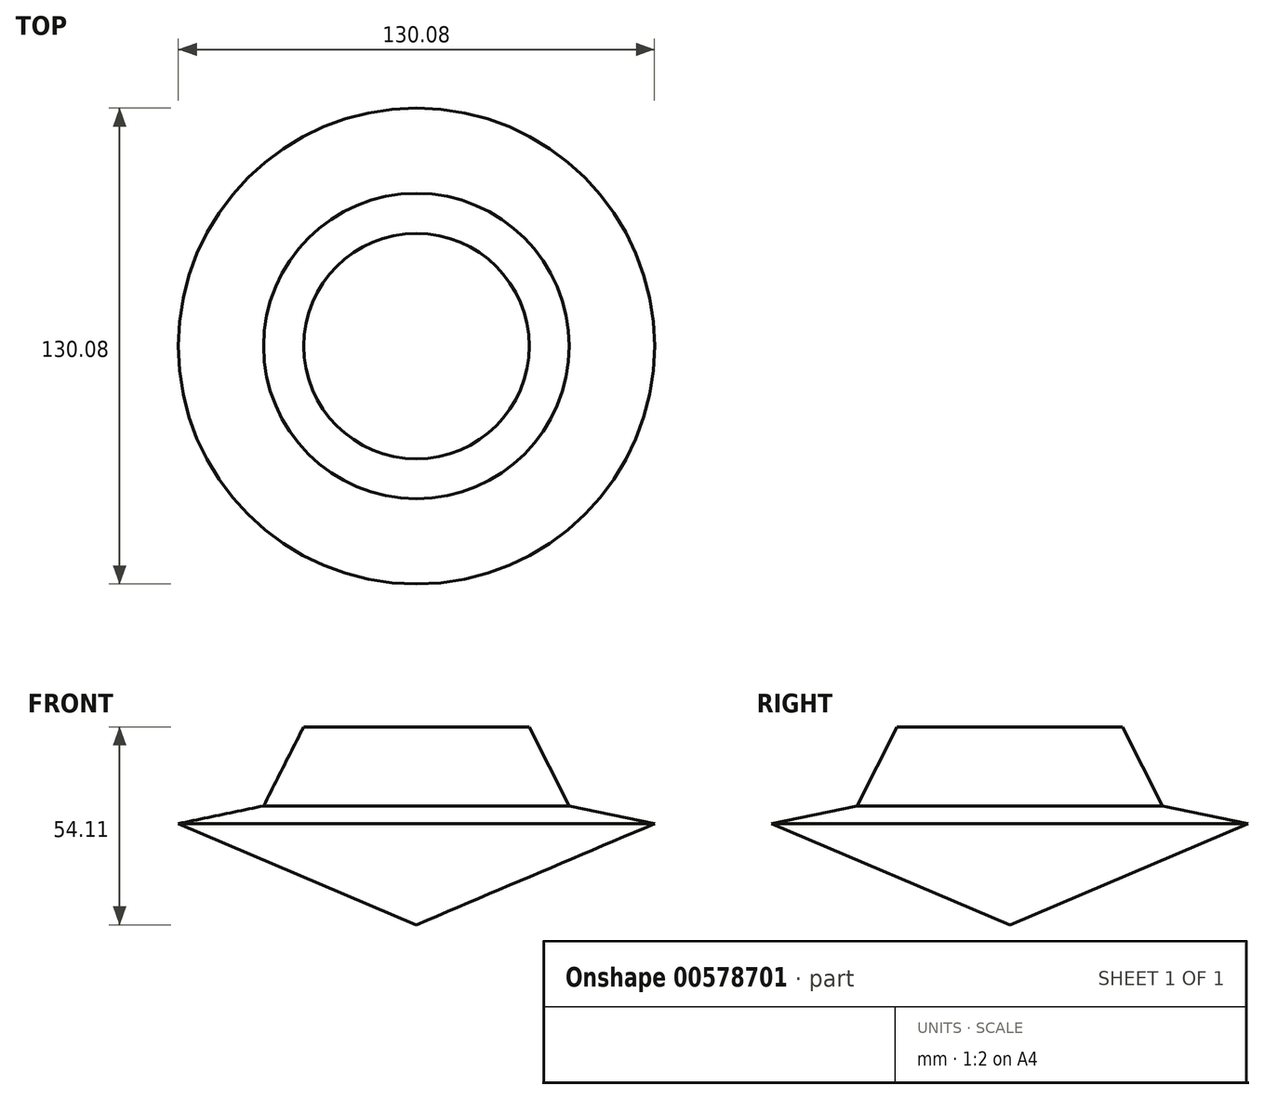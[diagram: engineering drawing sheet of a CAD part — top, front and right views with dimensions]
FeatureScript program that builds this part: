
annotation { "Feature Type Name" : "Feature", "Feature Type Description" : "" }
export const myFeature = defineFeature(function(context is Context, id is Id, definition is map)
    precondition{}
    {
        {
            var Q0;
            Q0=qCreatedBy(makeId("Front.planeOp"),FACE);
            var sketch = newSketch(context, id + "F0", { "sketchPlane" : qUnion([Q0])});
            skLineSegment(sketch, "E0", {"start": v(0, 0) * mm, "end": v(0, 54.1) * mm});
            skLineSegment(sketch, "E1", {"start": v(0, 54.1) * mm, "end": v(30.8, 54.1) * mm});
            skLineSegment(sketch, "E2", {"start": v(30.8, 54.1) * mm, "end": v(41.73, 32.52) * mm});
            skLineSegment(sketch, "E3", {"start": v(41.73, 32.52) * mm, "end": v(65.04, 27.63) * mm});
            skLineSegment(sketch, "E4", {"start": v(65.04, 27.63) * mm, "end": v(0, 0) * mm});
            skSolve(sketch);
        }
        {
            var Q0;
            Q0=makeQuery(id+"F0.imprint","IMPRINT",FACE,{"disambiguationData":[TD([[makeQuery(id+"F0.imprint","IMPRINT",EDGE,{"derivedFrom":sQuery(id+"F0.wireOp",EDGE,"E0")}),-1.0]])]});
            var Q1;
            Q1=sQuery(id+"F0.wireOp",EDGE,"E0");
            revolve(context, id + "F1", {"entities" : qUnion([Q0]), "axis" : qUnion([Q1]), "revolveType" : RevolveType.FULL});
        }
    });
